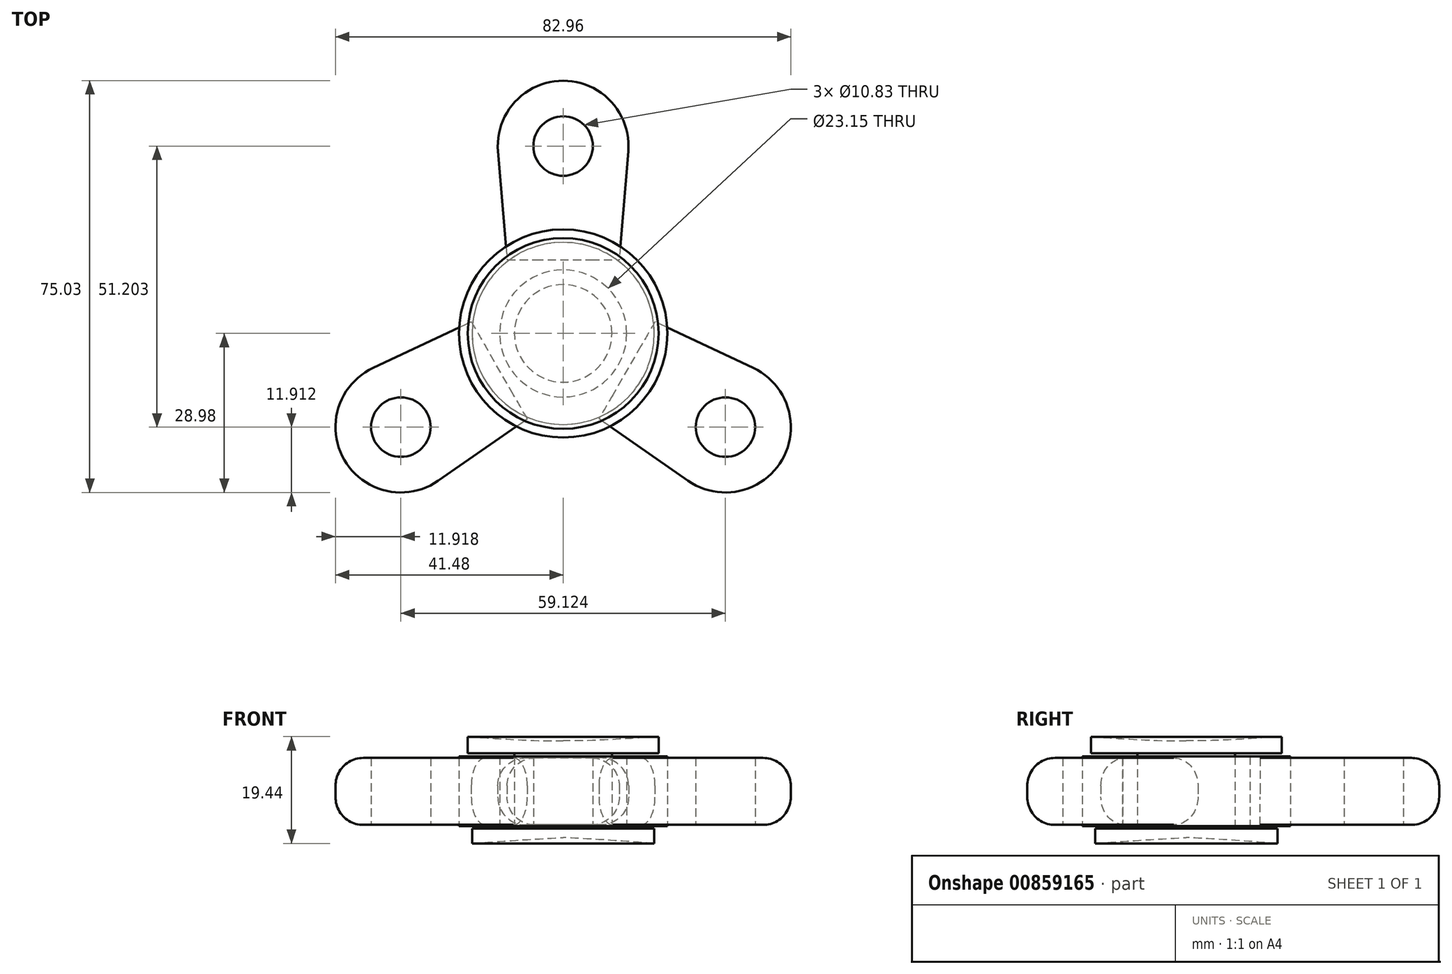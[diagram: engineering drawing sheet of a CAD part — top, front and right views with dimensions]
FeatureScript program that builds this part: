
annotation { "Feature Type Name" : "Feature", "Feature Type Description" : "" }
export const myFeature = defineFeature(function(context is Context, id is Id, definition is map)
    precondition{}
    {
        {
            var Q0;
            Q0=qCreatedBy(makeId("Top.planeOp"),FACE);
            var sketch = newSketch(context, id + "F0", { "sketchPlane" : qUnion([Q0])});
            skCircle(sketch, "E0", {"center": v(0, 34.14) * mm, "radius": 11.91 * mm});
            skLineSegment(sketch, "E1", {"start": v(-11.87, 33.14) * mm, "end": v(-10.21, 13.42) * mm});
            skLineSegment(sketch, "E2", {"start": v(11.87, 33.14) * mm, "end": v(10.21, 13.42) * mm});
            skLineSegment(sketch, "E3", {"start": v(-10.21, 13.42) * mm, "end": v(10.21, 13.42) * mm});
            skCircle(sketch, "E4", {"center": v(0, 34.14) * mm, "radius": 5.41 * mm});
            skSolve(sketch);
        }
        {
            var Q0;
            Q0 = qSketchRegion(id + "F0", true);
            extrude(context, id + "F1", {"entities" : qUnion([Q0]), "endBound" : BoundingType.SYMMETRIC, "depth" : 12.2 * mm, "offsetDistance" : 25.4 * mm});
        }
        {
            var Q0;
            Q0=qCreatedBy(makeId("Top.planeOp"),FACE);
            var sketch = newSketch(context, id + "F2", { "sketchPlane" : qUnion([Q0])});
            skCircle(sketch, "E5", {"center": v(0, 0) * mm, "radius": 23.55 * mm});
            skSolve(sketch);
        }
        {
            var Q0;
            Q0=makeQuery(id+"F1.opExtrude","SWEPT_BODY",BODY,{"disambiguationData":[OSD([sQuery(id+"F0.wireOp",EDGE,"E0"),sQuery(id+"F0.wireOp",EDGE,"E1"),sQuery(id+"F0.wireOp",EDGE,"E2"),sQuery(id+"F0.wireOp",EDGE,"E3"),sQuery(id+"F0.wireOp",EDGE,"E4")])]});
            var Q1;
            Q1=sQuery(id+"F2.wireOp",EDGE,"E5");
            circularPattern(context, id + "F3", {"entities" : qUnion([Q0]), "axis" : qUnion([Q1]), "angle" : 360 * degree, "instanceCount" : 3, "equalSpace" : true});
        }
        {
            var Q0;
            Q0=qCreatedBy(makeId("Top.planeOp"),FACE);
            var sketch = newSketch(context, id + "F4", { "sketchPlane" : qUnion([Q0])});
            skCircle(sketch, "E6", {"center": v(0, 0) * mm, "radius": 18.97 * mm});
            skCircle(sketch, "E7", {"center": v(0, 0) * mm, "radius": 11.58 * mm});
            skSolve(sketch);
        }
        {
            var Q0;
            Q0=makeQuery(id+"F4.imprint","IMPRINT",FACE,{"disambiguationData":[TD([[makeQuery(id+"F4.imprint","IMPRINT",EDGE,{"derivedFrom":sQuery(id+"F4.wireOp",EDGE,"E6")}),1.0]])]});
            extrude(context, id + "F5", {"entities" : qUnion([Q0]), "surfaceOperationType" : NewSurfaceOperationType.ADD, "endBound" : BoundingType.SYMMETRIC, "depth" : 12.7 * mm, "offsetDistance" : 25.4 * mm});
        }
        {
            var Q0;
            Q0=qCreatedBy(makeId("Right.planeOp"),FACE);
            var sketch = newSketch(context, id + "F6", { "sketchPlane" : qUnion([Q0])});
            skLineSegment(sketch, "E8", {"start": v(17.38, 9.97) * mm, "end": v(17.38, 6.93) * mm});
            skLineSegment(sketch, "E9", {"start": v(17.38, 6.93) * mm, "end": v(8.9, 6.93) * mm});
            skLineSegment(sketch, "E10", {"start": v(8.9, 6.93) * mm, "end": v(8.9, -6.75) * mm});
            skLineSegment(sketch, "E11", {"start": v(8.9, -6.75) * mm, "end": v(16.6, -6.75) * mm});
            skLineSegment(sketch, "E12", {"start": v(16.6, -6.75) * mm, "end": v(16.6, -9.47) * mm});
            skFitSpline(sketch, "E13", {"points": [v(17.38, 9.97) * mm, v(5.78, 9.3) * mm, v(0, 9.22) * mm], "startDerivative": vector(-21.5, -1.4) * mm, "endDerivative": vector(-12.77, -0.02) * mm});
            skFitSpline(sketch, "E14", {"points": [v(16.6, -9.47) * mm, v(5.78, -8.72) * mm, v(0, -8.42) * mm], "startDerivative": vector(-20.17, 1.46) * mm, "endDerivative": vector(-12.62, 0.61) * mm});
            skLineSegment(sketch, "E15", {"start": v(0, -8.42) * mm, "end": v(0, 9.22) * mm});
            skSolve(sketch);
        }
        {
            var Q0;
            Q0 = qSketchRegion(id + "F6", true);
            var Q1;
            Q1=sQuery(id+"F6.wireOp",EDGE,"E15");
            revolve(context, id + "F7", {"surfaceOperationType" : NewSurfaceOperationType.NEW, "entities" : qUnion([Q0]), "axis" : qUnion([Q1]), "revolveType" : RevolveType.FULL});
        }
        {
            var Q0;
            Q0=makeQuery(id+"F3.opPattern","COPY",EDGE,{"derivedFrom":makeQuery(id+"F1.opExtrude","CAP_EDGE",EDGE,{"disambiguationData":[OSD([sQuery(id+"F0.wireOp",EDGE,"E2")])],"isStart":true}),"instanceName":"1"});
            var Q1;
            Q1=makeQuery(id+"F3.opPattern","COPY",EDGE,{"derivedFrom":makeQuery(id+"F1.opExtrude","CAP_EDGE",EDGE,{"disambiguationData":[OSD([sQuery(id+"F0.wireOp",EDGE,"E2")])],"isStart":false}),"instanceName":"1"});
            var Q2;
            Q2=makeQuery(id+"F1.opExtrude","CAP_EDGE",EDGE,{"disambiguationData":[OSD([sQuery(id+"F0.wireOp",EDGE,"E1")])],"isStart":true});
            var Q3;
            Q3=makeQuery(id+"F1.opExtrude","CAP_EDGE",EDGE,{"disambiguationData":[OSD([sQuery(id+"F0.wireOp",EDGE,"E1")])],"isStart":false});
            var Q4;
            Q4=makeQuery(id+"F3.opPattern","COPY",EDGE,{"derivedFrom":makeQuery(id+"F1.opExtrude","CAP_EDGE",EDGE,{"disambiguationData":[OSD([sQuery(id+"F0.wireOp",EDGE,"E1")])],"isStart":true}),"instanceName":"2"});
            var Q5;
            Q5=makeQuery(id+"F3.opPattern","COPY",EDGE,{"derivedFrom":makeQuery(id+"F1.opExtrude","CAP_EDGE",EDGE,{"disambiguationData":[OSD([sQuery(id+"F0.wireOp",EDGE,"E1")])],"isStart":false}),"instanceName":"2"});
            fillet(context, id + "F8", {"entities" : qUnion([Q0, Q1, Q2, Q3, Q4, Q5]), "radius" : 5.08 * mm, "tangentPropagation" : true, "allowEdgeOverflow" : false});
        }
    });
